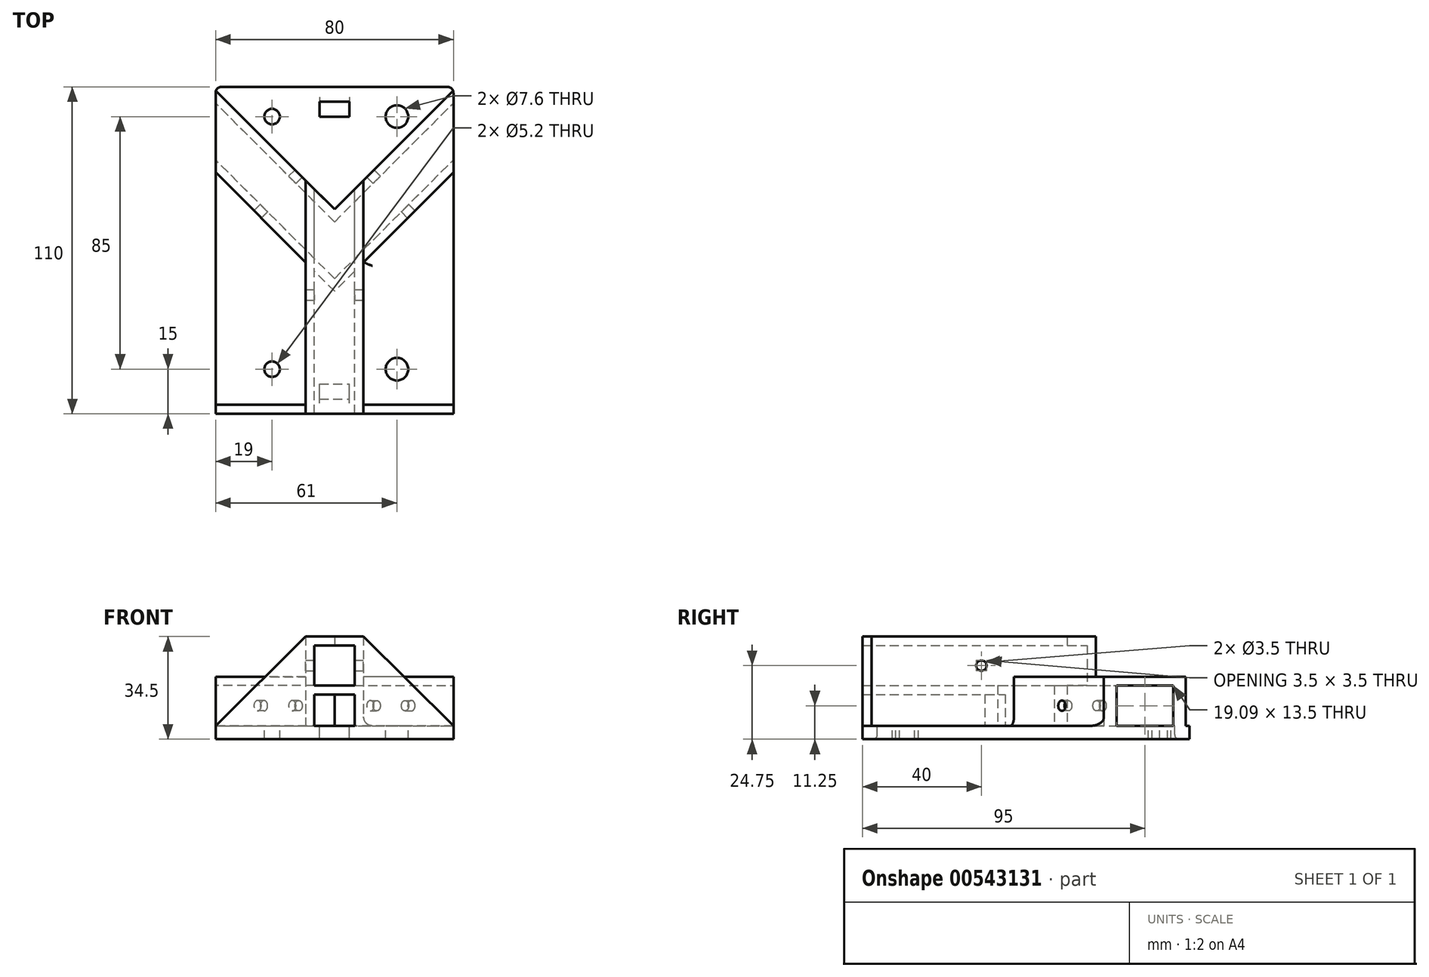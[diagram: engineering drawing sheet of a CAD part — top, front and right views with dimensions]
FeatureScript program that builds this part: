
annotation { "Feature Type Name" : "Feature", "Feature Type Description" : "" }
export const myFeature = defineFeature(function(context is Context, id is Id, definition is map)
    precondition{}
    {
        {
            var Q0;
            Q0=qCreatedBy(makeId("Top.planeOp"),FACE);
            var sketch = newSketch(context, id + "F0", { "sketchPlane" : qUnion([Q0])});
            skLineSegment(sketch, "E0.bottom", {"start": v(-40, 55) * mm, "end": v(40, 55) * mm});
            skLineSegment(sketch, "E0.top", {"start": v(-40, -55) * mm, "end": v(40, -55) * mm});
            skLineSegment(sketch, "E0.left", {"start": v(-40, 55) * mm, "end": v(-40, -55) * mm});
            skLineSegment(sketch, "E0.right", {"start": v(40, 55) * mm, "end": v(40, -55) * mm});
            skPoint(sketch, "E1", {"position": v(0, 55) * mm});
            skPoint(sketch, "E2", {"position": v(40, 0) * mm});
            skSolve(sketch);
        }
        {
            var Q0;
            Q0 = qSketchRegion(id + "F0", true);
            extrude(context, id + "F1", {"entities" : qUnion([Q0]), "depth" : 4.5 * mm, "offsetDistance" : 25 * mm});
        }
        {
            var Q0;
            Q0=makeQuery(id+"F1.opExtrude","CAP_FACE",FACE,{"disambiguationData":[OSD([sQuery(id+"F0.wireOp",EDGE,"E0.bottom"),sQuery(id+"F0.wireOp",EDGE,"E0.top"),sQuery(id+"F0.wireOp",EDGE,"E0.left"),sQuery(id+"F0.wireOp",EDGE,"E0.right")])],"isStart":false});
            var sketch = newSketch(context, id + "F2", { "sketchPlane" : qUnion([Q0])});
            skLineSegment(sketch, "E3.bottom", {"start": v(-5, 50) * mm, "end": v(5, 50) * mm});
            skLineSegment(sketch, "E3.top", {"start": v(-5, 45) * mm, "end": v(5, 45) * mm});
            skLineSegment(sketch, "E3.left", {"start": v(-5, 50) * mm, "end": v(-5, 45) * mm});
            skLineSegment(sketch, "E3.right", {"start": v(5, 50) * mm, "end": v(5, 45) * mm});
            skPoint(sketch, "E4", {"position": v(0, 50) * mm});
            skLineSegment(sketch, "E5.MirrorCS", {"start": v(5, -50) * mm, "end": v(5, -45) * mm});
            skPoint(sketch, "E6.MirrorP", {"position": v(0, -50) * mm});
            skLineSegment(sketch, "E7.MirrorCS", {"start": v(-5, -50) * mm, "end": v(5, -50) * mm});
            skLineSegment(sketch, "E8.MirrorCS", {"start": v(-5, -50) * mm, "end": v(-5, -45) * mm});
            skLineSegment(sketch, "E9.MirrorCS", {"start": v(-5, -45) * mm, "end": v(5, -45) * mm});
            skSolve(sketch);
        }
        {
            var Q0;
            Q0 = qSketchRegion(id + "F2", true);
            extrude(context, id + "F3", {"entities" : qUnion([Q0]), "operationType" : NewBodyOperationType.REMOVE, "endBound" : BoundingType.THROUGH_ALL, "oppositeDirection" : true, "depth" : 25 * mm, "offsetDistance" : 25 * mm});
        }
        {
            var Q0;
            Q0=makeQuery(id+"F1.opExtrude","CAP_FACE",FACE,{"disambiguationData":[OSD([sQuery(id+"F0.wireOp",EDGE,"E0.bottom"),sQuery(id+"F0.wireOp",EDGE,"E0.top"),sQuery(id+"F0.wireOp",EDGE,"E0.left"),sQuery(id+"F0.wireOp",EDGE,"E0.right")])],"isStart":false});
            var sketch = newSketch(context, id + "F4", { "sketchPlane" : qUnion([Q0])});
            skLineSegment(sketch, "E10", {"start": v(0, 0) * mm, "end": v(-55.66, 55.66) * mm, "construction": true});
            skLineSegment(sketch, "E11.MirrorCS", {"start": v(0, 0) * mm, "end": v(55.66, 55.66) * mm, "construction": true});
            skPoint(sketch, "E12.orphan", {"position": v(-19.52, -33.09) * mm});
            skPoint(sketch, "E13.right.end.orphan", {"position": v(19.52, -33.09) * mm});
            skLineSegment(sketch, "E14", {"start": v(0, -9.55) * mm, "end": v(40, 30.45) * mm});
            skLineSegment(sketch, "E15", {"start": v(40, 30.45) * mm, "end": v(40, 26.21) * mm});
            skLineSegment(sketch, "E16", {"start": v(40, 26.21) * mm, "end": v(9.75, -4.04) * mm});
            skLineSegment(sketch, "E17", {"start": v(0, 9.55) * mm, "end": v(40, 49.55) * mm});
            skLineSegment(sketch, "E18", {"start": v(40, 49.55) * mm, "end": v(40, 53.79) * mm});
            skLineSegment(sketch, "E19", {"start": v(40, 53.79) * mm, "end": v(0, 13.79) * mm});
            skLineSegment(sketch, "E20.MirrorCS", {"start": v(-40, 53.79) * mm, "end": v(0, 13.79) * mm});
            skLineSegment(sketch, "E21.MirrorCS", {"start": v(-40, 49.55) * mm, "end": v(-40, 53.79) * mm});
            skLineSegment(sketch, "E22.MirrorCS", {"start": v(0, 9.55) * mm, "end": v(-40, 49.55) * mm});
            skLineSegment(sketch, "E23.MirrorCS", {"start": v(0, -9.55) * mm, "end": v(-40, 30.45) * mm});
            skLineSegment(sketch, "E24.MirrorCS", {"start": v(-40, 30.45) * mm, "end": v(-40, 26.21) * mm});
            skLineSegment(sketch, "E25.MirrorCS", {"start": v(-40, 26.21) * mm, "end": v(-9.75, -4.04) * mm});
            skLineSegment(sketch, "E26", {"start": v(-6.75, -55) * mm, "end": v(-6.75, -7.04) * mm});
            skLineSegment(sketch, "E27", {"start": v(-9.75, -4.04) * mm, "end": v(-9.75, -55) * mm});
            skLineSegment(sketch, "E28", {"start": v(-9.75, -55) * mm, "end": v(-6.75, -55) * mm});
            skLineSegment(sketch, "E29.MirrorCS", {"start": v(9.75, -4.04) * mm, "end": v(9.75, -55) * mm});
            skLineSegment(sketch, "E30.MirrorCS", {"start": v(9.75, -55) * mm, "end": v(6.75, -55) * mm});
            skLineSegment(sketch, "E31.MirrorCS", {"start": v(6.75, -55) * mm, "end": v(6.75, -7.04) * mm});
            skLineSegment(sketch, "E32.trimOffspring", {"start": v(-6.75, -7.04) * mm, "end": v(0, -13.79) * mm});
            skLineSegment(sketch, "E33.trimOffspring", {"start": v(6.75, -7.04) * mm, "end": v(0, -13.79) * mm});
            skSolve(sketch);
        }
        {
            var Q0;
            Q0 = qSketchRegion(id + "F4", true);
            extrude(context, id + "F5", {"entities" : qUnion([Q0]), "operationType" : NewBodyOperationType.ADD, "depth" : 13.5 * mm, "offsetDistance" : 25 * mm});
        }
        {
            var Q0;
            {var subQ2=sQuery(id+"F0.wireOp",EDGE,"E0.right");var subQ3=makeQuery(id+"F1.opExtrude","SWEPT_FACE",FACE,{"disambiguationData":[OSD([subQ2])]});var subQ4=sQuery(id+"F0.wireOp",EDGE,"E0.top");var subQ5=makeQuery(id+"F1.opExtrude","SWEPT_FACE",FACE,{"disambiguationData":[OSD([subQ4])]});var subQ6=sQuery(id+"F0.wireOp",EDGE,"E0.left");Q0=makeQuery(id+"FRnbRCNZirlfwO5_1.boolean.opBoolean","SPLIT",FACE,{"disambiguationData":[TD([subQ3])],"derivedFrom":makeQuery(id+"F2k25GQCj0JztAD_1.boolean.opBoolean","SPLIT",FACE,{"disambiguationData":[TD([subQ5])],"derivedFrom":makeQuery(id+"F1.opExtrude","CAP_FACE",FACE,{"disambiguationData":[OSD([sQuery(id+"F0.wireOp",EDGE,"E0.bottom"),subQ4,subQ6,subQ2])],"isStart":false})})});}
            var sketch = newSketch(context, id + "F6", { "sketchPlane" : qUnion([Q0])});
            skCircle(sketch, "E34", {"center": v(21, -40) * mm, "radius": 3.8 * mm});
            skCircle(sketch, "E35", {"center": v(21, 45) * mm, "radius": 3.8 * mm});
            skCircle(sketch, "E36", {"center": v(-21, 45) * mm, "radius": 2.6 * mm});
            skCircle(sketch, "E37", {"center": v(-21, -40) * mm, "radius": 2.6 * mm});
            skSolve(sketch);
        }
        {
            var Q0;
            Q0 = qSketchRegion(id + "F6", true);
            extrude(context, id + "F7", {"entities" : qUnion([Q0]), "operationType" : NewBodyOperationType.REMOVE, "endBound" : BoundingType.THROUGH_ALL, "oppositeDirection" : true, "depth" : 25 * mm, "offsetDistance" : 25 * mm});
        }
        {
            var Q0;
            {var subQ0=sQuery(id+"F0.wireOp",EDGE,"E0.top");Q0=makeQuery(id+"F5.boolean.opBoolean","SPLIT",FACE,{"disambiguationData":[TD([makeQuery(id+"F3.boolean.opBoolean","COPY",FACE,{"derivedFrom":makeQuery(id+"F3.opExtrude","SWEPT_FACE",FACE,{"disambiguationData":[OSD([sQuery(id+"F2.wireOp",EDGE,"E5.MirrorCS")])]})})])],"derivedFrom":makeQuery(id+"F1.opExtrude","CAP_FACE",FACE,{"disambiguationData":[OSD([sQuery(id+"F0.wireOp",EDGE,"E0.bottom"),subQ0,sQuery(id+"F0.wireOp",EDGE,"E0.left"),sQuery(id+"F0.wireOp",EDGE,"E0.right")])],"isStart":false})});}
            cPlane(context, id + "F8", {"entities" : qUnion([Q0]), "cplaneType" : CPlaneType.OFFSET, "offset" : 13.5 * mm, "width" : 150 * mm, "height" : 150 * mm});
        }
        {
            var Q0;
            Q0=makeQuery(id+"F5.opExtrude","CAP_FACE",FACE,{"disambiguationData":[OSD([sQuery(id+"F4.wireOp",EDGE,"E14"),sQuery(id+"F4.wireOp",EDGE,"E15"),sQuery(id+"F4.wireOp",EDGE,"E16"),sQuery(id+"F4.wireOp",EDGE,"E23.MirrorCS"),sQuery(id+"F4.wireOp",EDGE,"E24.MirrorCS"),sQuery(id+"F4.wireOp",EDGE,"E25.MirrorCS"),sQuery(id+"F4.wireOp",EDGE,"E26"),sQuery(id+"F4.wireOp",EDGE,"E27"),sQuery(id+"F4.wireOp",EDGE,"E28"),sQuery(id+"F4.wireOp",EDGE,"E29.MirrorCS"),sQuery(id+"F4.wireOp",EDGE,"E30.MirrorCS"),sQuery(id+"F4.wireOp",EDGE,"E31.MirrorCS"),sQuery(id+"F4.wireOp",EDGE,"E32.trimOffspring"),sQuery(id+"F4.wireOp",EDGE,"E33.trimOffspring")])],"isStart":false});
            var sketch = newSketch(context, id + "F9", { "sketchPlane" : qUnion([Q0])});
            skLineSegment(sketch, "E38", {"start": v(-9.75, -55) * mm, "end": v(-9.75, 23.54) * mm});
            skLineSegment(sketch, "E39", {"start": v(-9.75, -55) * mm, "end": v(-6.75, -55) * mm});
            skLineSegment(sketch, "E40", {"start": v(-6.75, -55) * mm, "end": v(-6.75, 20.54) * mm});
            skLineSegment(sketch, "E41", {"start": v(-6.75, 20.54) * mm, "end": v(-9.75, 23.54) * mm});
            skLineSegment(sketch, "E42.MirrorCS", {"start": v(6.75, 20.54) * mm, "end": v(9.75, 23.54) * mm});
            skLineSegment(sketch, "E43.MirrorCS", {"start": v(9.75, -55) * mm, "end": v(6.75, -55) * mm});
            skLineSegment(sketch, "E44.MirrorCS", {"start": v(9.75, -55) * mm, "end": v(9.75, 23.54) * mm});
            skLineSegment(sketch, "E45.MirrorCS", {"start": v(6.75, -55) * mm, "end": v(6.75, 20.54) * mm});
            skSolve(sketch);
        }
        {
            var Q0;
            Q0 = qSketchRegion(id + "F9", true);
            extrude(context, id + "F10", {"entities" : qUnion([Q0]), "operationType" : NewBodyOperationType.ADD, "depth" : 13.5 * mm, "offsetDistance" : 25 * mm});
        }
        {
            var Q0;
            {var subQ0=sQuery(id+"F4.wireOp",EDGE,"E15");var subQ1=sQuery(id+"F4.wireOp",EDGE,"E14");var subQ2=sQuery(id+"F4.wireOp",EDGE,"E16");var subQ4=sQuery(id+"F4.wireOp",EDGE,"E29.MirrorCS");Q0=makeQuery(id+"F10.boolean.opBoolean","SPLIT",FACE,{"disambiguationData":[TD([makeQuery(id+"F1.opExtrude","SWEPT_FACE",FACE,{"disambiguationData":[OSD([sQuery(id+"F0.wireOp",EDGE,"E0.right")])]})])],"derivedFrom":makeQuery(id+"F5.opExtrude","CAP_FACE",FACE,{"disambiguationData":[OSD([subQ1,subQ0,subQ2,sQuery(id+"F4.wireOp",EDGE,"E23.MirrorCS"),sQuery(id+"F4.wireOp",EDGE,"E24.MirrorCS"),sQuery(id+"F4.wireOp",EDGE,"E25.MirrorCS"),sQuery(id+"F4.wireOp",EDGE,"E26"),sQuery(id+"F4.wireOp",EDGE,"E27"),sQuery(id+"F4.wireOp",EDGE,"E28"),subQ4,sQuery(id+"F4.wireOp",EDGE,"E30.MirrorCS"),sQuery(id+"F4.wireOp",EDGE,"E31.MirrorCS"),sQuery(id+"F4.wireOp",EDGE,"E32.trimOffspring"),sQuery(id+"F4.wireOp",EDGE,"E33.trimOffspring")])],"isStart":false})});}
            var sketch = newSketch(context, id + "F11", { "sketchPlane" : qUnion([Q0])});
            skLineSegment(sketch, "E46", {"start": v(9.75, -4.04) * mm, "end": v(40, 26.21) * mm});
            skLineSegment(sketch, "E47", {"start": v(40, 26.21) * mm, "end": v(40, 53.79) * mm});
            skLineSegment(sketch, "E48", {"start": v(40, 53.79) * mm, "end": v(9.75, 23.54) * mm});
            skLineSegment(sketch, "E49", {"start": v(9.75, 23.54) * mm, "end": v(9.75, -4.04) * mm});
            skLineSegment(sketch, "E50.MirrorCS", {"start": v(-40, 26.21) * mm, "end": v(-40, 53.79) * mm});
            skLineSegment(sketch, "E51.MirrorCS", {"start": v(-9.75, -4.04) * mm, "end": v(-40, 26.21) * mm});
            skLineSegment(sketch, "E52.MirrorCS", {"start": v(-40, 53.79) * mm, "end": v(-9.75, 23.54) * mm});
            skLineSegment(sketch, "E53.MirrorCS", {"start": v(-9.75, 23.54) * mm, "end": v(-9.75, -4.04) * mm});
            skSolve(sketch);
        }
        {
            var Q0;
            Q0 = qSketchRegion(id + "F11", true);
            extrude(context, id + "F12", {"entities" : qUnion([Q0]), "operationType" : NewBodyOperationType.ADD, "depth" : 3 * mm, "offsetDistance" : 25 * mm});
        }
        {
            var Q0;
            Q0=qCreatedBy(id+"F8.planeOp",FACE);
            var sketch = newSketch(context, id + "F13", { "sketchPlane" : qUnion([Q0])});
            skLineSegment(sketch, "E54", {"start": v(-6.75, -7.04) * mm, "end": v(-6.75, -55) * mm});
            skLineSegment(sketch, "E55", {"start": v(-6.75, -55) * mm, "end": v(6.75, -55) * mm});
            skLineSegment(sketch, "E56", {"start": v(6.75, -55) * mm, "end": v(6.75, -7.04) * mm});
            skLineSegment(sketch, "E57", {"start": v(6.75, -7.04) * mm, "end": v(0, -13.79) * mm});
            skLineSegment(sketch, "E58", {"start": v(0, -13.79) * mm, "end": v(-6.75, -7.04) * mm});
            skSolve(sketch);
        }
        {
            var Q0;
            Q0 = qSketchRegion(id + "F13", true);
            extrude(context, id + "F14", {"entities" : qUnion([Q0]), "operationType" : NewBodyOperationType.ADD, "oppositeDirection" : true, "depth" : 3 * mm, "offsetDistance" : 25 * mm});
        }
        {
            var Q0;
            Q0=makeQuery(id+"F10.opExtrude","CAP_FACE",FACE,{"disambiguationData":[OSD([sQuery(id+"F9.wireOp",EDGE,"E38"),sQuery(id+"F9.wireOp",EDGE,"E39"),sQuery(id+"F9.wireOp",EDGE,"E40"),sQuery(id+"F9.wireOp",EDGE,"E41")])],"isStart":false});
            var sketch = newSketch(context, id + "F15", { "sketchPlane" : qUnion([Q0])});
            skLineSegment(sketch, "E59", {"start": v(-9.75, -55) * mm, "end": v(-9.75, 23.54) * mm});
            skLineSegment(sketch, "E60", {"start": v(-9.75, 23.54) * mm, "end": v(0, 13.79) * mm});
            skLineSegment(sketch, "E61", {"start": v(0, 13.79) * mm, "end": v(9.75, 23.54) * mm});
            skLineSegment(sketch, "E62", {"start": v(9.75, 23.54) * mm, "end": v(9.75, -55) * mm});
            skLineSegment(sketch, "E63", {"start": v(9.75, -55) * mm, "end": v(-9.75, -55) * mm});
            skSolve(sketch);
        }
        {
            var Q0;
            Q0 = qSketchRegion(id + "F15", true);
            extrude(context, id + "F16", {"entities" : qUnion([Q0]), "operationType" : NewBodyOperationType.ADD, "depth" : 3 * mm, "offsetDistance" : 25 * mm});
        }
        {
            var Q0;
            Q0=makeQuery(id+"F16.boolean.opBoolean","MERGE",FACE,{"derivedFrom":[makeQuery(id+"F10.boolean.opBoolean","MERGE",FACE,{"derivedFrom":[makeQuery(id+"F5.opExtrude","SWEPT_FACE",FACE,{"disambiguationData":[OSD([sQuery(id+"F4.wireOp",EDGE,"E29.MirrorCS")])]}),makeQuery(id+"F10.opExtrude","SWEPT_FACE",FACE,{"disambiguationData":[OSD([sQuery(id+"F9.wireOp",EDGE,"E44.MirrorCS")])]})]}),makeQuery(id+"F16.opExtrude","SWEPT_FACE",FACE,{"disambiguationData":[OSD([sQuery(id+"F15.wireOp",EDGE,"E62")])]})]});
            var sketch = newSketch(context, id + "F17", { "sketchPlane" : qUnion([Q0])});
            skCircle(sketch, "E64", {"center": v(-15, 24.75) * mm, "radius": 1.75 * mm});
            skSolve(sketch);
        }
        {
            var Q0;
            Q0 = qSketchRegion(id + "F17", true);
            extrude(context, id + "F18", {"entities" : qUnion([Q0]), "operationType" : NewBodyOperationType.REMOVE, "endBound" : BoundingType.THROUGH_ALL, "oppositeDirection" : true, "depth" : 25 * mm, "offsetDistance" : 25 * mm});
        }
        {
            var Q0;
            Q0=makeQuery(id+"F12.boolean.opBoolean","MERGE",FACE,{"derivedFrom":[makeQuery(id+"F5.opExtrude","SWEPT_FACE",FACE,{"disambiguationData":[OSD([sQuery(id+"F4.wireOp",EDGE,"E16")])]}),makeQuery(id+"F12.opExtrude","SWEPT_FACE",FACE,{"disambiguationData":[OSD([sQuery(id+"F11.wireOp",EDGE,"E46")])]})]});
            var sketch = newSketch(context, id + "F19", { "sketchPlane" : qUnion([Q0])});
            skCircle(sketch, "E65", {"center": v(26.82, 11.25) * mm, "radius": 1.75 * mm});
            skSolve(sketch);
        }
        {
            var Q0;
            Q0 = qSketchRegion(id + "F19", true);
            extrude(context, id + "F20", {"entities" : qUnion([Q0]), "operationType" : NewBodyOperationType.REMOVE, "endBound" : BoundingType.THROUGH_ALL, "oppositeDirection" : true, "depth" : 25 * mm, "offsetDistance" : 25 * mm});
        }
        {
            var Q0;
            Q0=makeQuery(id+"F12.boolean.opBoolean","MERGE",FACE,{"derivedFrom":[makeQuery(id+"F5.opExtrude","SWEPT_FACE",FACE,{"disambiguationData":[OSD([sQuery(id+"F4.wireOp",EDGE,"E25.MirrorCS")])]}),makeQuery(id+"F12.opExtrude","SWEPT_FACE",FACE,{"disambiguationData":[OSD([sQuery(id+"F11.wireOp",EDGE,"E51.MirrorCS")])]})]});
            var sketch = newSketch(context, id + "F21", { "sketchPlane" : qUnion([Q0])});
            skCircle(sketch, "E66", {"center": v(-26.82, 11.25) * mm, "radius": 1.75 * mm});
            skSolve(sketch);
        }
        {
            var Q0;
            Q0 = qSketchRegion(id + "F21", true);
            extrude(context, id + "F22", {"entities" : qUnion([Q0]), "operationType" : NewBodyOperationType.REMOVE, "endBound" : BoundingType.THROUGH_ALL, "oppositeDirection" : true, "depth" : 25 * mm, "offsetDistance" : 25 * mm});
        }
        {
            var Q0;
            Q0=makeQuery(id+"F16.boolean.opBoolean","MERGE",FACE,{"derivedFrom":[makeQuery(id+"FgTDKjpBSp7kaUr_1.boolean.opBoolean","MERGE",FACE,{"derivedFrom":[makeQuery(id+"F10.boolean.opBoolean","MERGE",FACE,{"derivedFrom":[makeQuery(id+"F5.boolean.opBoolean","MERGE",FACE,{"derivedFrom":[makeQuery(id+"F1.opExtrude","SWEPT_FACE",FACE,{"disambiguationData":[OSD([sQuery(id+"F0.wireOp",EDGE,"E0.top")])]}),makeQuery(id+"F5.opExtrude","SWEPT_FACE",FACE,{"disambiguationData":[OSD([sQuery(id+"F4.wireOp",EDGE,"E28")])]}),makeQuery(id+"F5.opExtrude","SWEPT_FACE",FACE,{"disambiguationData":[OSD([sQuery(id+"F4.wireOp",EDGE,"E30.MirrorCS")])]})]}),makeQuery(id+"F10.opExtrude","SWEPT_FACE",FACE,{"disambiguationData":[OSD([sQuery(id+"F9.wireOp",EDGE,"E39")])]}),makeQuery(id+"F10.opExtrude","SWEPT_FACE",FACE,{"disambiguationData":[OSD([sQuery(id+"F9.wireOp",EDGE,"E43.MirrorCS")])]})]}),makeQuery(id+"FgTDKjpBSp7kaUr_1.opExtrude","SWEPT_FACE",FACE,{"disambiguationData":[OSD([sQuery(id+"FmViRON45fdqLzS_1.wireOp",EDGE,"BDJIcsjL-xs4u-wPTx-RrfS-JACAWXZk00vl")])]})]}),makeQuery(id+"F16.opExtrude","SWEPT_FACE",FACE,{"disambiguationData":[OSD([sQuery(id+"F15.wireOp",EDGE,"E63")])]})]});
            var sketch = newSketch(context, id + "F23", { "sketchPlane" : qUnion([Q0])});
            skLineSegment(sketch, "E67", {"start": v(9.75, 34.5) * mm, "end": v(40, 4.5) * mm});
            skLineSegment(sketch, "E68", {"start": v(40, 4.5) * mm, "end": v(9.75, 4.5) * mm});
            skLineSegment(sketch, "E69", {"start": v(9.75, 4.5) * mm, "end": v(9.75, 34.5) * mm});
            skLineSegment(sketch, "E70.MirrorCS", {"start": v(-9.75, 4.5) * mm, "end": v(-9.75, 34.5) * mm});
            skLineSegment(sketch, "E71.MirrorCS", {"start": v(-9.75, 34.5) * mm, "end": v(-40, 4.5) * mm});
            skLineSegment(sketch, "E72.MirrorCS", {"start": v(-40, 4.5) * mm, "end": v(-9.75, 4.5) * mm});
            skSolve(sketch);
        }
        {
            var Q0;
            Q0 = qSketchRegion(id + "F23", true);
            extrude(context, id + "F24", {"entities" : qUnion([Q0]), "operationType" : NewBodyOperationType.ADD, "oppositeDirection" : true, "depth" : 3 * mm, "offsetDistance" : 25 * mm});
        }
        {
            var Q0;
            Q0=makeQuery(id+"F3.boolean.opBoolean","COPY",EDGE,{"derivedFrom":makeQuery(id+"F3.opExtrude","CAP_EDGE",EDGE,{"disambiguationData":[OSD([sQuery(id+"F2.wireOp",EDGE,"E3.bottom")])],"isStart":true})});
            var Q1;
            Q1=makeQuery(id+"F3.boolean.opBoolean","INTERSECT",EDGE,{"derivedFrom":[makeQuery(id+"F1.opExtrude","CAP_FACE",FACE,{"disambiguationData":[OSD([sQuery(id+"F0.wireOp",EDGE,"E0.bottom"),sQuery(id+"F0.wireOp",EDGE,"E0.top"),sQuery(id+"F0.wireOp",EDGE,"E0.left"),sQuery(id+"F0.wireOp",EDGE,"E0.right")])],"isStart":true}),makeQuery(id+"F3.opExtrude","SWEPT_FACE",FACE,{"disambiguationData":[OSD([sQuery(id+"F2.wireOp",EDGE,"E3.bottom")])]})]});
            var Q2;
            Q2=makeQuery(id+"F3.boolean.opBoolean","INTERSECT",EDGE,{"derivedFrom":[makeQuery(id+"F1.opExtrude","CAP_FACE",FACE,{"disambiguationData":[OSD([sQuery(id+"F0.wireOp",EDGE,"E0.bottom"),sQuery(id+"F0.wireOp",EDGE,"E0.top"),sQuery(id+"F0.wireOp",EDGE,"E0.left"),sQuery(id+"F0.wireOp",EDGE,"E0.right")])],"isStart":true}),makeQuery(id+"F3.opExtrude","SWEPT_FACE",FACE,{"disambiguationData":[OSD([sQuery(id+"F2.wireOp",EDGE,"E7.MirrorCS")])]})]});
            var Q3;
            Q3=makeQuery(id+"F3.boolean.opBoolean","COPY",EDGE,{"derivedFrom":makeQuery(id+"F3.opExtrude","CAP_EDGE",EDGE,{"disambiguationData":[OSD([sQuery(id+"F2.wireOp",EDGE,"E7.MirrorCS")])],"isStart":true})});
            fillet(context, id + "F25", {"entities" : qUnion([Q0, Q1, Q2, Q3]), "radius" : 1.5 * mm, "tangentPropagation" : true, "allowEdgeOverflow" : false});
        }
        {
            var Q0;
            Q0=makeQuery(id+"F24.opExtrude","CAP_EDGE",EDGE,{"disambiguationData":[OSD([sQuery(id+"F23.wireOp",EDGE,"E70.MirrorCS")])],"isStart":false});
            var Q1;
            Q1=makeQuery(id+"F12.opExtrude","CAP_EDGE",EDGE,{"disambiguationData":[OSD([sQuery(id+"F11.wireOp",EDGE,"E53.MirrorCS")])],"isStart":false});
            var Q2;
            Q2=makeQuery(id+"F5.opExtrude","CAP_EDGE",EDGE,{"disambiguationData":[OSD([sQuery(id+"F4.wireOp",EDGE,"E27")])],"isStart":true});
            var Q3;
            Q3=makeQuery(id+"F24.opExtrude","CAP_EDGE",EDGE,{"disambiguationData":[OSD([sQuery(id+"F23.wireOp",EDGE,"E72.MirrorCS")])],"isStart":false});
            var Q4;
            Q4=makeQuery(id+"F12.boolean.opBoolean","MERGE",EDGE,{"derivedFrom":[makeQuery(id+"F5.opExtrude","SWEPT_EDGE",EDGE,{"disambiguationData":[OSD([sQuery(id+"F4.wireOp",EDGE,"E25.MirrorCS"),sQuery(id+"F4.wireOp",EDGE,"E27")])]}),makeQuery(id+"F12.opExtrude","SWEPT_EDGE",EDGE,{"disambiguationData":[OSD([sQuery(id+"F11.wireOp",EDGE,"E51.MirrorCS"),sQuery(id+"F11.wireOp",EDGE,"E53.MirrorCS")])]})]});
            var Q5;
            Q5=makeQuery(id+"F5.opExtrude","CAP_EDGE",EDGE,{"disambiguationData":[OSD([sQuery(id+"F4.wireOp",EDGE,"E25.MirrorCS")])],"isStart":true});
            var Q6;
            Q6=makeQuery(id+"F24.opExtrude","CAP_EDGE",EDGE,{"disambiguationData":[OSD([sQuery(id+"F23.wireOp",EDGE,"E68")])],"isStart":false});
            var Q7;
            Q7=makeQuery(id+"F24.opExtrude","CAP_EDGE",EDGE,{"disambiguationData":[OSD([sQuery(id+"F23.wireOp",EDGE,"E69")])],"isStart":false});
            var Q8;
            Q8=makeQuery(id+"F5.opExtrude","CAP_EDGE",EDGE,{"disambiguationData":[OSD([sQuery(id+"F4.wireOp",EDGE,"E29.MirrorCS")])],"isStart":true});
            var Q9;
            Q9=makeQuery(id+"F12.boolean.opBoolean","MERGE",EDGE,{"derivedFrom":[makeQuery(id+"F5.opExtrude","SWEPT_EDGE",EDGE,{"disambiguationData":[OSD([sQuery(id+"F4.wireOp",EDGE,"E16"),sQuery(id+"F4.wireOp",EDGE,"E29.MirrorCS")])]}),makeQuery(id+"F12.opExtrude","SWEPT_EDGE",EDGE,{"disambiguationData":[OSD([sQuery(id+"F11.wireOp",EDGE,"E46"),sQuery(id+"F11.wireOp",EDGE,"E49")])]})]});
            var Q10;
            Q10=makeQuery(id+"F12.opExtrude","CAP_EDGE",EDGE,{"disambiguationData":[OSD([sQuery(id+"F11.wireOp",EDGE,"E49")])],"isStart":false});
            var Q11;
            Q11=makeQuery(id+"F5.opExtrude","CAP_EDGE",EDGE,{"disambiguationData":[OSD([sQuery(id+"F4.wireOp",EDGE,"E16")])],"isStart":true});
            fillet(context, id + "F26", {"entities" : qUnion([Q0, Q1, Q2, Q3, Q4, Q5, Q6, Q7, Q8, Q9, Q10, Q11]), "radius" : 3 * mm, "tangentPropagation" : true, "allowEdgeOverflow" : false});
        }
        {
            var Q0;
            Q0=makeQuery(id+"F1.opExtrude","SWEPT_EDGE",EDGE,{"disambiguationData":[OSD([sQuery(id+"F0.wireOp",EDGE,"E0.bottom"),sQuery(id+"F0.wireOp",EDGE,"E0.left")])]});
            var Q1;
            Q1=makeQuery(id+"F1.opExtrude","SWEPT_EDGE",EDGE,{"disambiguationData":[OSD([sQuery(id+"F0.wireOp",EDGE,"E0.bottom"),sQuery(id+"F0.wireOp",EDGE,"E0.right")])]});
            fillet(context, id + "F27", {"entities" : qUnion([Q0, Q1]), "radius" : 2 * mm, "tangentPropagation" : true, "allowEdgeOverflow" : false});
        }
    });
